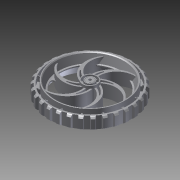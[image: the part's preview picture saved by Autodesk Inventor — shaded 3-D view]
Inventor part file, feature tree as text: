
AUTODESK INVENTOR PART (.ipt)
format: ipt  version: 2013 (Build 170138000, 138)  size: 1,323,520 bytes
history: native  units: mm (DEFAULTED — no unit token found)
features: imported_body x1, sketch x1, other x1, extrude x1
ambient origin geometry x8: Origin, YZ Plane, XZ Plane, XY Plane, X Axis, Y Axis, Z Axis, Center Point
bodies: Solid1 (feature_tree)
feature tree (4):
  imported_body  "Base1"
  sketch  "Sketch1"  dims[d0=25.4mm d1=0.0mm d2=0.0mm d3=0.0mm]
  other  "Srf1"
  extrude  "ExtrusionSrf1"  TaperAngle=0.0deg  [1 undecoded]
note: 1 required parameter value undecoded (feature->parameter linkage not recoverable at this tier; creation-order binding heuristic only, values carry confidence <= 0.55)
